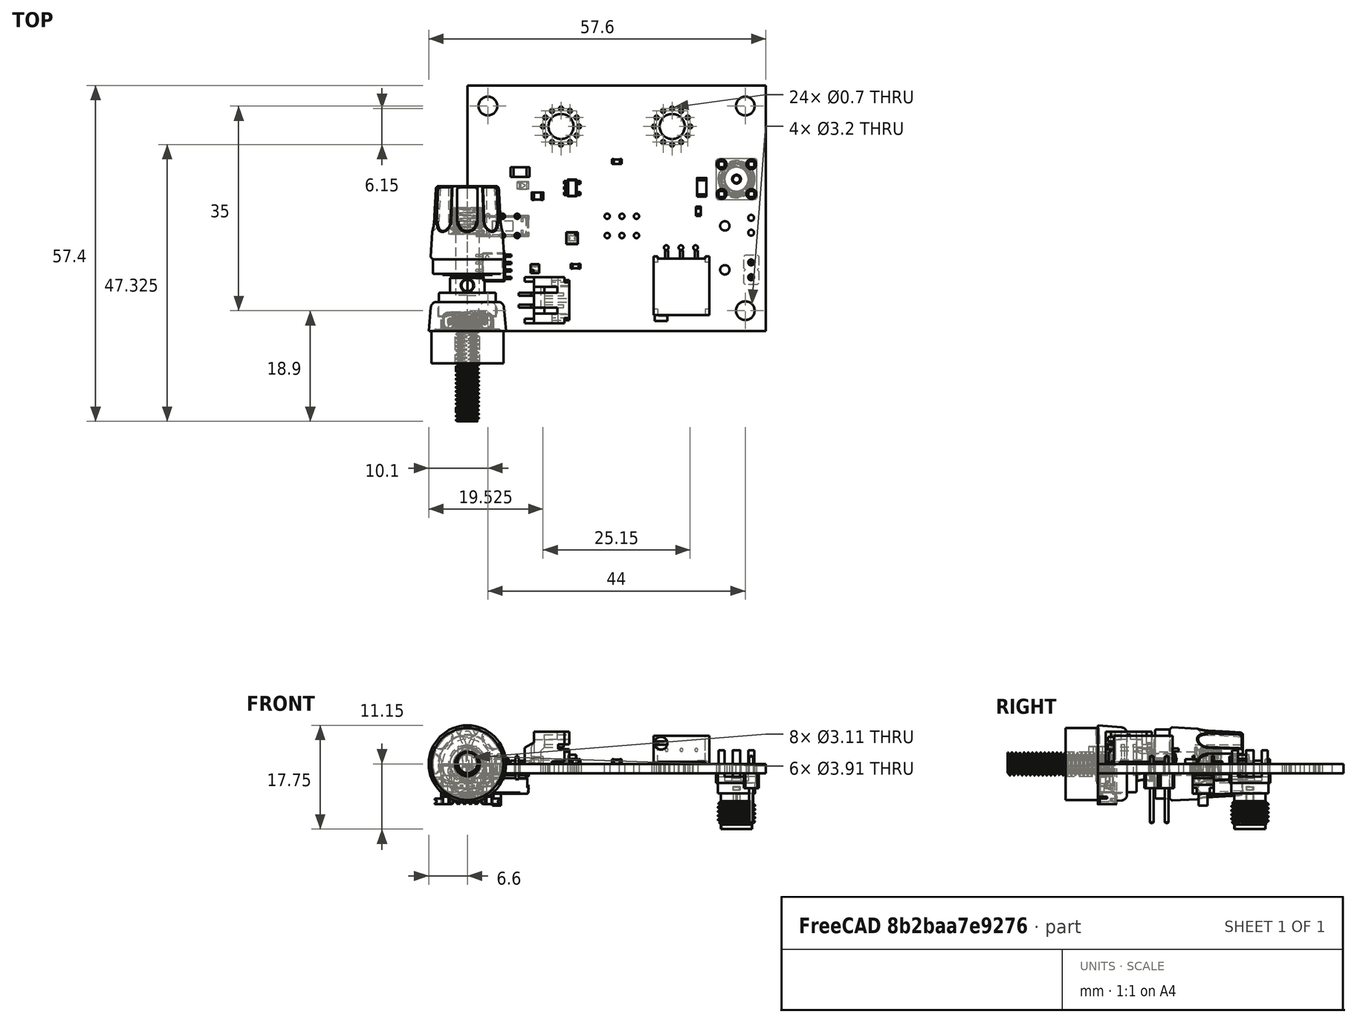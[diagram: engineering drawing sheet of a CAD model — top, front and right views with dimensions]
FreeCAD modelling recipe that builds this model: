
FCSTD DOCUMENT  (FreeCAD 0.20R29603 (Git))
Label: SCuSA_RevB1_PCBA
License: All rights reserved
LicenseURL: http://en.wikipedia.org/wiki/All_rights_reserved
objects: App::Link×39, Part::Feature×25, App::Part×11, PartDesign::CoordinateSystem×1, Sketcher::SketchObject×1
note: 27 computed .brp shape members not serialized (recipe doc carries the construction recipe); baked Part::Feature solids carry a one-line shape summary decoded from their .brp

FEATURE [PartDesign::CoordinateSystem] Local_CS_3e51
  AttacherType = Attacher::AttachEngine3D
  MapMode = 2
  Support = -> [X_Axis001]
FEATURE [Part::Feature] Pcb_3e51
  Placement = pos=(-112,104,0) rot=(0,0,1;0rad)
  shape: bbox 51 x 42 x 1.6 mm, 64 faces (baked)
FEATURE [Sketcher::SketchObject] PCB_Sketch_3e51
  FullyConstrained = false
  sketch-geometry (4):
    g0: LineSegment StartX=51 StartY=0 StartZ=0 EndX=0 EndY=0 EndZ=0
    g1: LineSegment StartX=0 StartY=42 StartZ=0 EndX=51 EndY=42 EndZ=0
    g2: LineSegment StartX=0 StartY=0 StartZ=0 EndX=0 EndY=42 EndZ=0
    g3: LineSegment StartX=51 StartY=42 StartZ=0 EndX=51 EndY=0 EndZ=0
  constraints (4):
    c: Coincident(g0,g2)
    c: Coincident(g1,g2)
    c: Coincident(g0,g3)
    c: Coincident(g1,g3)
FEATURE [App::Part] Board_Geoms_3e51
  Group = -> [Pcb_3e51,PCB_Sketch_3e51]
  Origin = -> Origin
FEATURE [Part::Feature] Shape  label="R118_R_1206_3216Metric_9a429e010c18"
  Placement = pos=(40.05,24.6,0) rot=(0,0,1;1.5708rad)
  shape: bbox 1.6 x 3.2 x 0.55 mm, 26 faces (baked)
FEATURE [Part::Feature] Shape001  label="C110_C_0603_1608Metric_07e89f88e059"
  Placement = pos=(25.55,29,0) rot=(0,0,1;3.14159rad)
  shape: bbox 1.6 x 0.8 x 0.8 mm, 28 faces (baked)
FEATURE [Part::Feature] Shape002  label="R121_R_0603_1608Metric_cabd63930a75"
  Placement = pos=(39.5,20.5,0) rot=(0,0,-1;1.5708rad)
  shape: bbox 0.8 x 1.6 x 0.45 mm, 26 faces (baked)
FEATURE [Part::Feature] Shape003  label="F101_Fuse_1206_3216Metric_160eb9ee9b08"
  Placement = pos=(9,27.2,0) rot=(0,0,1;0rad)
  shape: bbox 3.2 x 1.6 x 0.55 mm, 26 faces (baked)
FEATURE [Part::Feature] Shape004  label="U103_SOT_23_5_5ae0390f21ab"
  Placement = pos=(17.9,24.5,0) rot=(0,0,1;0rad)
  shape: bbox 2.8 x 2.9 x 1.55 mm, 109 faces (baked)
FEATURE [Part::Feature] Shape005  label="C101_C_0805_2012Metric_832099bd49ec"
  Placement = pos=(12,23.1,0) rot=(0,0,1;3.14159rad)
  shape: bbox 2 x 1.25 x 1.25 mm, 28 faces (baked)
FEATURE [App::Link] R121_R_0603_1608Metric_cabd63930a75_ln_  label="R103_R_0603_1608Metric_e52815511993"
  LinkPlacement = pos=(8.4,22.9,0) rot=(0,0,1;3.14159rad)
  LinkedObject = -> Shape002
  Placement = pos=(8.4,22.9,0) rot=(0,0,1;3.14159rad)
FEATURE [App::Link] R121_R_0603_1608Metric_cabd63930a75_ln_001  label="R123_R_0603_1608Metric_c2d5c197cd85"
  LinkPlacement = pos=(18.3,19.9,0) rot=(0,0,1;3.14159rad)
  LinkedObject = -> Shape002
  Placement = pos=(18.3,19.9,0) rot=(0,0,1;3.14159rad)
FEATURE [App::Link] R121_R_0603_1608Metric_cabd63930a75_ln_002  label="R117_R_0603_1608Metric_1370ab284e11"
  LinkPlacement = pos=(4.5,21.6,0) rot=(0,0,1;3.14159rad)
  LinkedObject = -> Shape002
  Placement = pos=(4.5,21.6,0) rot=(0,0,1;3.14159rad)
FEATURE [App::Link] R121_R_0603_1608Metric_cabd63930a75_ln_003  label="R105_R_0603_1608Metric_8828eca0330c"
  LinkPlacement = pos=(12.2,14.3,0) rot=(0,0,1;3.14159rad)
  LinkedObject = -> Shape002
  Placement = pos=(12.2,14.3,0) rot=(0,0,1;3.14159rad)
FEATURE [App::Link] C101_C_0805_2012Metric_832099bd49ec_ln_  label="C102_C_0805_2012Metric_9881d72c0956"
  LinkPlacement = pos=(12,16.9,0) rot=(0,0,1;3.14159rad)
  LinkedObject = -> Shape005
  Placement = pos=(12,16.9,0) rot=(0,0,1;3.14159rad)
FEATURE [App::Link] C110_C_0603_1608Metric_07e89f88e059_ln_  label="C111_C_0603_1608Metric_e0c0d5fa783b"
  LinkPlacement = pos=(22.2,29,0) rot=(0,0,1;3.14159rad)
  LinkedObject = -> Shape001
  Placement = pos=(22.2,29,0) rot=(0,0,1;3.14159rad)
FEATURE [App::Link] C110_C_0603_1608Metric_07e89f88e059_ln_001  label="C106_C_0603_1608Metric_96d47e7760c2"
  LinkPlacement = pos=(18.3,18.3,0) rot=(0,0,1;0rad)
  LinkedObject = -> Shape001
  Placement = pos=(18.3,18.3,0) rot=(0,0,1;0rad)
FEATURE [App::Link] C110_C_0603_1608Metric_07e89f88e059_ln_002  label="C109_C_0603_1608Metric_a759c64c54e8"
  LinkPlacement = pos=(28.9,29,0) rot=(0,0,1;3.14159rad)
  LinkedObject = -> Shape001
  Placement = pos=(28.9,29,0) rot=(0,0,1;3.14159rad)
FEATURE [App::Link] C110_C_0603_1608Metric_07e89f88e059_ln_003  label="C115_C_0603_1608Metric_735d576579cb"
  LinkPlacement = pos=(28.9,22,0) rot=(0,0,1;0rad)
  LinkedObject = -> Shape001
  Placement = pos=(28.9,22,0) rot=(0,0,1;0rad)
FEATURE [App::Link] C101_C_0805_2012Metric_832099bd49ec_ln_001  label="C108_C_0805_2012Metric_e86135985600"
  LinkPlacement = pos=(18.5,13.3,0) rot=(0,0,1;0rad)
  LinkedObject = -> Shape005
  Placement = pos=(18.5,13.3,0) rot=(0,0,1;0rad)
FEATURE [Part::Feature] Shape006  label="Q101_SOIC_8_39x49mm_P127mm_18785c1fbfb3"
  Placement = pos=(4.5,11,0) rot=(0,0,1;0rad)
  shape: bbox 6 x 4.9 x 1.75 mm, 156 faces (baked)
FEATURE [App::Link] R121_R_0603_1608Metric_cabd63930a75_ln_004  label="R109_R_0603_1608Metric_f4df95fcec91"
  LinkPlacement = pos=(14.9,24.5,0) rot=(0,0,1;1.5708rad)
  LinkedObject = -> Shape002
  Placement = pos=(14.9,24.5,0) rot=(0,0,1;1.5708rad)
FEATURE [App::Link] C110_C_0603_1608Metric_07e89f88e059_ln_004  label="C116_C_0603_1608Metric_dd78862adcb4"
  LinkPlacement = pos=(20.7,25.2,0) rot=(0,0,1;1.5708rad)
  LinkedObject = -> Shape001
  Placement = pos=(20.7,25.2,0) rot=(0,0,1;1.5708rad)
FEATURE [App::Link] C101_C_0805_2012Metric_832099bd49ec_ln_002  label="C114_C_0805_2012Metric_a4eab3955a47"
  LinkPlacement = pos=(15.5,15.9,0) rot=(0,0,1;1.5708rad)
  LinkedObject = -> Shape005
  Placement = pos=(15.5,15.9,0) rot=(0,0,1;1.5708rad)
FEATURE [Part::Feature] Shape007  label="J102_S2B-PH-SM4_327a573b422f"
  Placement = pos=(0.4,-2.6,0) rot=(0.57735,0.57735,0.57735;2.0944rad)
  shape: bbox 8.6 x 7.9 x 5.6 mm, 88 faces (baked)
FEATURE [App::Link] R121_R_0603_1608Metric_cabd63930a75_ln_005  label="R115_R_0603_1608Metric_e91c1c194d21"
  LinkPlacement = pos=(26.3,31.5,0) rot=(0,0,-1;1.5708rad)
  LinkedObject = -> Shape002
  Placement = pos=(26.3,31.5,0) rot=(0,0,-1;1.5708rad)
FEATURE [Part::Feature] Part__Feature  label="USB4135-GF-A"
  shape: bbox 11.15 x 3.257 x 6.907 mm, 318 faces (baked)
FEATURE [Part::Feature] Part__Feature001  label="USB4135-GF-A001"
  shape: bbox 8.3 x 2.985 x 6.55 mm, 467 faces (baked)
FEATURE [App::Part] USB4135_GF_A  label="J101_USB4135-GF-A002_08b6693a03fd"
  Group = -> [Part__Feature,Part__Feature001]
  Origin = -> Origin008
  Placement = pos=(-1.5175,29.25,0) rot=(0.57735,-0.57735,-0.57735;2.0944rad)
FEATURE [Part::Feature] Shape008  label="U111_WSON_8_1EP_2x2mm_P05mm_EP09x16mm_bf8e54cc5a9e"
  Placement = pos=(17.9,15.9,0) rot=(0,0,-1;1.5708rad)
  shape: bbox 1.98 x 2 x 0.82 mm, 62 faces (baked)
FEATURE [Part::Feature] Shape009  label="FB100_L_0603_1608Metric_5c9160750dc1"
  Placement = pos=(18.5,11.1,0) rot=(0,0,1;0rad)
  shape: bbox 1.6 x 0.8 x 0.8 mm, 28 faces (baked)
FEATURE [App::Link] R118_R_1206_3216Metric_9a429e010c18_ln_  label="R114_R_1206_3216Metric_9449b8210d6c"
  LinkPlacement = pos=(25.5,34.35,0) rot=(0,0,1;3.14159rad)
  LinkedObject = -> Shape
  Placement = pos=(25.5,34.35,0) rot=(0,0,1;3.14159rad)
FEATURE [App::Link] R121_R_0603_1608Metric_cabd63930a75_ln_006  label="R102_R_0603_1608Metric_428a7ca26184"
  LinkPlacement = pos=(8.2,29.15,0) rot=(0,0,1;0rad)
  LinkedObject = -> Shape002
  Placement = pos=(8.2,29.15,0) rot=(0,0,1;0rad)
FEATURE [App::Link] C110_C_0603_1608Metric_07e89f88e059_ln_005  label="C113_C_0603_1608Metric_c568501282b4"
  LinkPlacement = pos=(36.6,27.1,0) rot=(0,0,1;0rad)
  LinkedObject = -> Shape001
  Placement = pos=(36.6,27.1,0) rot=(0,0,1;0rad)
FEATURE [App::Link] R121_R_0603_1608Metric_cabd63930a75_ln_007  label="R116_R_0603_1608Metric_7018264d671d"
  LinkPlacement = pos=(24.8,31.5,0) rot=(0,0,-1;1.5708rad)
  LinkedObject = -> Shape002
  Placement = pos=(24.8,31.5,0) rot=(0,0,-1;1.5708rad)
FEATURE [App::Link] C110_C_0603_1608Metric_07e89f88e059_ln_006  label="C112_C_0603_1608Metric_2f680c3bccde"
  LinkPlacement = pos=(25.55,22,0) rot=(0,0,1;3.14159rad)
  LinkedObject = -> Shape001
  Placement = pos=(25.55,22,0) rot=(0,0,1;3.14159rad)
FEATURE [App::Link] R121_R_0603_1608Metric_cabd63930a75_ln_008  label="R101_R_0603_1608Metric_6d1fb4459d4d"
  LinkPlacement = pos=(8.2,30.7,0) rot=(0,0,1;0rad)
  LinkedObject = -> Shape002
  Placement = pos=(8.2,30.7,0) rot=(0,0,1;0rad)
FEATURE [App::Link] C110_C_0603_1608Metric_07e89f88e059_ln_007  label="C121_C_0603_1608Metric_b24aff25157a"
  LinkPlacement = pos=(41,20.5,0) rot=(0,0,1;1.5708rad)
  LinkedObject = -> Shape001
  Placement = pos=(41,20.5,0) rot=(0,0,1;1.5708rad)
FEATURE [App::Link] C110_C_0603_1608Metric_07e89f88e059_ln_008  label="C120_C_0603_1608Metric_3728ccd4f199"
  LinkPlacement = pos=(15.8,22,0) rot=(0,0,1;3.14159rad)
  LinkedObject = -> Shape001
  Placement = pos=(15.8,22,0) rot=(0,0,1;3.14159rad)
FEATURE [Part::Feature] Shape010  label="RV101_Cut_b268e7737479"
  Placement = pos=(41.55,23.79,6.4) rot=(0,0.707107,-0.707107;3.14159rad)
  shape: bbox 9.53 x 12.05 x 4.83 mm, 32 faces (baked)
FEATURE [App::Link] Q101_SOIC_8_39x49mm_P127mm_18785c1fbfb3_ln_  label="U105_SOIC_8_39x49mm_P127mm_81b4a2160633"
  LinkPlacement = pos=(25.55,25.5,0) rot=(0,0,1;0rad)
  LinkedObject = -> Shape006
  Placement = pos=(25.55,25.5,0) rot=(0,0,1;0rad)
FEATURE [App::Link] R121_R_0603_1608Metric_cabd63930a75_ln_009  label="R122_R_0603_1608Metric_47ff7c3b82b1"
  LinkPlacement = pos=(6.6,33.9125,0) rot=(0,0,-1;1.5708rad)
  LinkedObject = -> Shape002
  Placement = pos=(6.6,33.9125,0) rot=(0,0,-1;1.5708rad)
FEATURE [App::Link] C110_C_0603_1608Metric_07e89f88e059_ln_009  label="C103_C_0603_1608Metric_b43a54b29ec9"
  LinkPlacement = pos=(12.2,12.7,0) rot=(0,0,1;0rad)
  LinkedObject = -> Shape001
  Placement = pos=(12.2,12.7,0) rot=(0,0,1;0rad)
FEATURE [App::Link] R121_R_0603_1608Metric_cabd63930a75_ln_010  label="R104_R_0603_1608Metric_4504fa6f6234"
  LinkPlacement = pos=(12.9,26.3,0) rot=(0,0,1;1.5708rad)
  LinkedObject = -> Shape002
  Placement = pos=(12.9,26.3,0) rot=(0,0,1;1.5708rad)
FEATURE [App::Link] Q101_SOIC_8_39x49mm_P127mm_18785c1fbfb3_ln_001  label="U106_SOIC_8_39x49mm_P127mm_f8bf6cf0ab73"
  LinkPlacement = pos=(34.95,23.6,0) rot=(0,0,1;0rad)
  LinkedObject = -> Shape006
  Placement = pos=(34.95,23.6,0) rot=(0,0,1;0rad)
FEATURE [App::Link] U103_SOT_23_5_5ae0390f21ab_ln_  label="U101_SOT_23_5_b81ba866f2ca"
  LinkPlacement = pos=(12,20,0) rot=(0,0,1;1.5708rad)
  LinkedObject = -> Shape004
  Placement = pos=(12,20,0) rot=(0,0,1;1.5708rad)
FEATURE [App::Link] R121_R_0603_1608Metric_cabd63930a75_ln_011  label="R108_R_0603_1608Metric_1a3b190c03d7"
  LinkPlacement = pos=(4.7,7.5,0) rot=(0,0,1;0rad)
  LinkedObject = -> Shape002
  Placement = pos=(4.7,7.5,0) rot=(0,0,1;0rad)
FEATURE [Part::Feature] Shape011  label="U102_WSON6_15x15mm_Pitch05mm_e3a42ca1607c"
  Placement = pos=(11.55,10.7,0) rot=(0,0,1;1.5708rad)
  shape: bbox 1.48 x 1.5 x 0.77 mm, 44 faces (baked)
FEATURE [App::Link] C101_C_0805_2012Metric_832099bd49ec_ln_003  label="C119_C_0805_2012Metric_dbd71c4523cc"
  LinkPlacement = pos=(21.5,12.3,0) rot=(0,0,1;1.5708rad)
  LinkedObject = -> Shape005
  Placement = pos=(21.5,12.3,0) rot=(0,0,1;1.5708rad)
FEATURE [App::Link] R121_R_0603_1608Metric_cabd63930a75_ln_012  label="R106_R_0603_1608Metric_9dcb38f3090e"
  LinkPlacement = pos=(9.4,12.35,0) rot=(0,0,1;1.5708rad)
  LinkedObject = -> Shape002
  Placement = pos=(9.4,12.35,0) rot=(0,0,1;1.5708rad)
FEATURE [App::Link] R121_R_0603_1608Metric_cabd63930a75_ln_013  label="R120_R_0603_1608Metric_a775436f9ad3"
  LinkPlacement = pos=(20.9,15.1,0) rot=(0,0,1;3.14159rad)
  LinkedObject = -> Shape002
  Placement = pos=(20.9,15.1,0) rot=(0,0,1;3.14159rad)
FEATURE [App::Link] R121_R_0603_1608Metric_cabd63930a75_ln_014  label="R107_R_0603_1608Metric_02283ed4e356"
  LinkPlacement = pos=(4.7,14.5,0) rot=(0,0,1;3.14159rad)
  LinkedObject = -> Shape002
  Placement = pos=(4.7,14.5,0) rot=(0,0,1;3.14159rad)
FEATURE [App::Link] R121_R_0603_1608Metric_cabd63930a75_ln_015  label="R119_R_0603_1608Metric_d680dbf24c9f"
  LinkPlacement = pos=(20.9,16.7,0) rot=(0,0,1;3.14159rad)
  LinkedObject = -> Shape002
  Placement = pos=(20.9,16.7,0) rot=(0,0,1;3.14159rad)
FEATURE [App::Part] Top_3e51
  Group = -> [Shape,Shape001,Shape002,Shape003,Shape004,Shape005,R121_R_0603_1608Metric_cabd63930a75_ln_,R121_R_0603_1608Metric_cabd63930a75_ln_001,R121_R_0603_1608Metric_cabd63930a75_ln_002,R121_R_0603_1608Metric_cabd63930a75_ln_003,C101_C_0805_2012Metric_832099bd49ec_ln_,C110_C_0603_1608Metric_07e89f88e059_ln_,C110_C_0603_1608Metric_07e89f88e059_ln_001,C110_C_0603_1608Metric_07e89f88e059_ln_002,+33 more]
  Origin = -> Origin003
FEATURE [Part::Feature] Shape012  label="J108_PinHeader_1x02_P254mm_Vertical_696c06d13264"
  Placement = pos=(48.5,9.225,-1.6) rot=(1,0,0;3.14159rad)
  shape: bbox 2.54 x 5.08 x 11.54 mm, 52 faces (baked)
FEATURE [Part::Feature] Shape013  label="SW101_CuK_JS202011CQN_DPDT_straight_5f730d750727"
  Placement = pos=(8.5075,19.65,-1.6) rot=(0,1,0;3.14159rad)
  shape: bbox 9 x 3.61 x 8.5 mm, 178 faces (baked)
FEATURE [App::Link] SW101_CuK_JS202011CQN_DPDT_straight_5f730d750727_ln_  label="SW102_CuK_JS202011CQN_DPDT_straight_acea3379d2f1"
  LinkPlacement = pos=(28.9075,19.65,-1.6) rot=(0,1,0;3.14159rad)
  LinkedObject = -> Shape013
  Placement = pos=(28.9075,19.65,-1.6) rot=(0,1,0;3.14159rad)
FEATURE [Part::Feature] Shape014  label="J105_60312002114503_f594866c6ba6"
  Placement = pos=(46,26,-3.25) rot=(0,0,1;3.14159rad)
  shape: bbox 7.319 x 7.009 x 13.51 mm, 77 faces (baked)
FEATURE [Part::Feature] Shape015  label="D102_LED_0805_2012Metric_8af6430a5faa"
  Placement = pos=(9.5,24.9,-1.6) rot=(0,1,0;3.14159rad)
  shape: bbox 2 x 1.25 x 1.1 mm, 50 faces (baked)
FEATURE [Part::Feature] Part__Feature002  label="TestPoint_Loop_D2_60mm_Drill1_6mm_Beaded_cp"
  shape: bbox 3.2 x 3.2 x 3 mm, 4 faces (baked)
FEATURE [Part::Feature] Part__Feature003  label="TestPoint_Loop_D2_60mm_Drill1_6mm_Beaded_cp001"
  shape: bbox 3.649 x 1.14 x 9.307 mm, 7 faces (baked)
FEATURE [App::Part] TestPoint_Loop_D2_60mm_Drill1_6mm_Beaded_cp  label="TP108_TestPoint_Loop_D2_60mm_Drill1_6mm_Beaded_cp002_35738ac4b5fc"
  Group = -> [Part__Feature002,Part__Feature003]
  Origin = -> Origin009
  Placement = pos=(44,18,-1.6) rot=(0.707107,0.707107,0;3.14159rad)
FEATURE [App::Link] D102_LED_0805_2012Metric_8af6430a5faa_ln_  label="D111_LED_0805_2012Metric_6c738512c6b0"
  LinkPlacement = pos=(9.5,22.7,-1.6) rot=(0,1,0;3.14159rad)
  LinkedObject = -> Shape015
  Placement = pos=(9.5,22.7,-1.6) rot=(0,1,0;3.14159rad)
FEATURE [Part::Feature] Part__Feature004  label="Fusion"
  shape: bbox 13.53 x 40.44 x 13.53 mm, 185 faces (baked)
FEATURE [Part::Feature] Part__Feature005  label="Fusion001"
  shape: bbox 13.52 x 10.5 x 13.52 mm, 10 faces (baked)
FEATURE [App::Part] Fusion  label="J103_Fusion002_9d3f900d180c"
  Group = -> [Part__Feature004,Part__Feature005]
  Origin = -> Origin010
  Placement = pos=(35,35,-7.1) rot=(-0.57735,0.57735,-0.57735;2.0944rad)
FEATURE [App::Link] D102_LED_0805_2012Metric_8af6430a5faa_ln_001  label="D101_LED_0805_2012Metric_902e5ca3932e"
  LinkPlacement = pos=(9.5,27.1,-1.6) rot=(0,1,0;3.14159rad)
  LinkedObject = -> Shape015
  Placement = pos=(9.5,27.1,-1.6) rot=(0,1,0;3.14159rad)
FEATURE [App::Link] J108_PinHeader_1x02_P254mm_Vertical_696c06d13264_ln_  label="J107_PinHeader_1x02_P254mm_Vertical_b8f4a2ff9044"
  LinkPlacement = pos=(48.5,16.845,-1.6) rot=(1,0,0;3.14159rad)
  LinkedObject = -> Shape012
  Placement = pos=(48.5,16.845,-1.6) rot=(1,0,0;3.14159rad)
FEATURE [App::Link] TP108_TestPoint_Loop_D2_60mm_Drill1_6mm_Beaded_cp002_35738ac4b5fc_ln_  label="TP107_TestPoint_Loop_D2_60mm_Drill1_6mm_Beaded_cp002_804a37e84f20"
  LinkPlacement = pos=(44,10.5,-1.6) rot=(0.707107,0.707107,0;3.14159rad)
  LinkedObject = -> TestPoint_Loop_D2_60mm_Drill1_6mm_Beaded_cp
  Placement = pos=(44,10.5,-1.6) rot=(0.707107,0.707107,0;3.14159rad)
FEATURE [App::Part] Bot_3e51
  Group = -> [Shape012,Shape013,SW101_CuK_JS202011CQN_DPDT_straight_5f730d750727_ln_,Shape014,Shape015,TestPoint_Loop_D2_60mm_Drill1_6mm_Beaded_cp,D102_LED_0805_2012Metric_8af6430a5faa_ln_,D102_LED_0805_2012Metric_8af6430a5faa_ln_001,J108_PinHeader_1x02_P254mm_Vertical_696c06d13264_ln_,TP108_TestPoint_Loop_D2_60mm_Drill1_6mm_Beaded_cp002_35738ac4b5fc_ln_]
  Origin = -> Origin004
FEATURE [App::Part] Step_Models_3e51
  Group = -> [Top_3e51,Bot_3e51]
  Origin = -> Origin002
FEATURE [Part::Feature] Part__Feature006  label="Fusion002"
  shape: bbox 13.53 x 40.44 x 13.53 mm, 185 faces (baked)
FEATURE [Part::Feature] Part__Feature007  label="Fusion003"
  shape: bbox 13.52 x 10.5 x 13.52 mm, 10 faces (baked)
FEATURE [App::Part] Fusion001  label="J104_Fusion004_39d20d171dee"
  Group = -> [Part__Feature006,Part__Feature007]
  Origin = -> Origin011
  Placement = pos=(16,35,-7.1) rot=(-0.57735,0.57735,-0.57735;2.0944rad)
FEATURE [App::Part] BotV_3e51
  Group = -> [Fusion,Fusion001]
  Origin = -> Origin007
FEATURE [App::Part] Step_Virtual_Models_3e51
  Group = -> [BotV_3e51]
  Origin = -> Origin005
FEATURE [App::Part] Board_3e51  label="SCuSA"
  Group = -> [Local_CS_3e51,Board_Geoms_3e51,Step_Models_3e51,Step_Virtual_Models_3e51]
  Origin = -> Origin001
